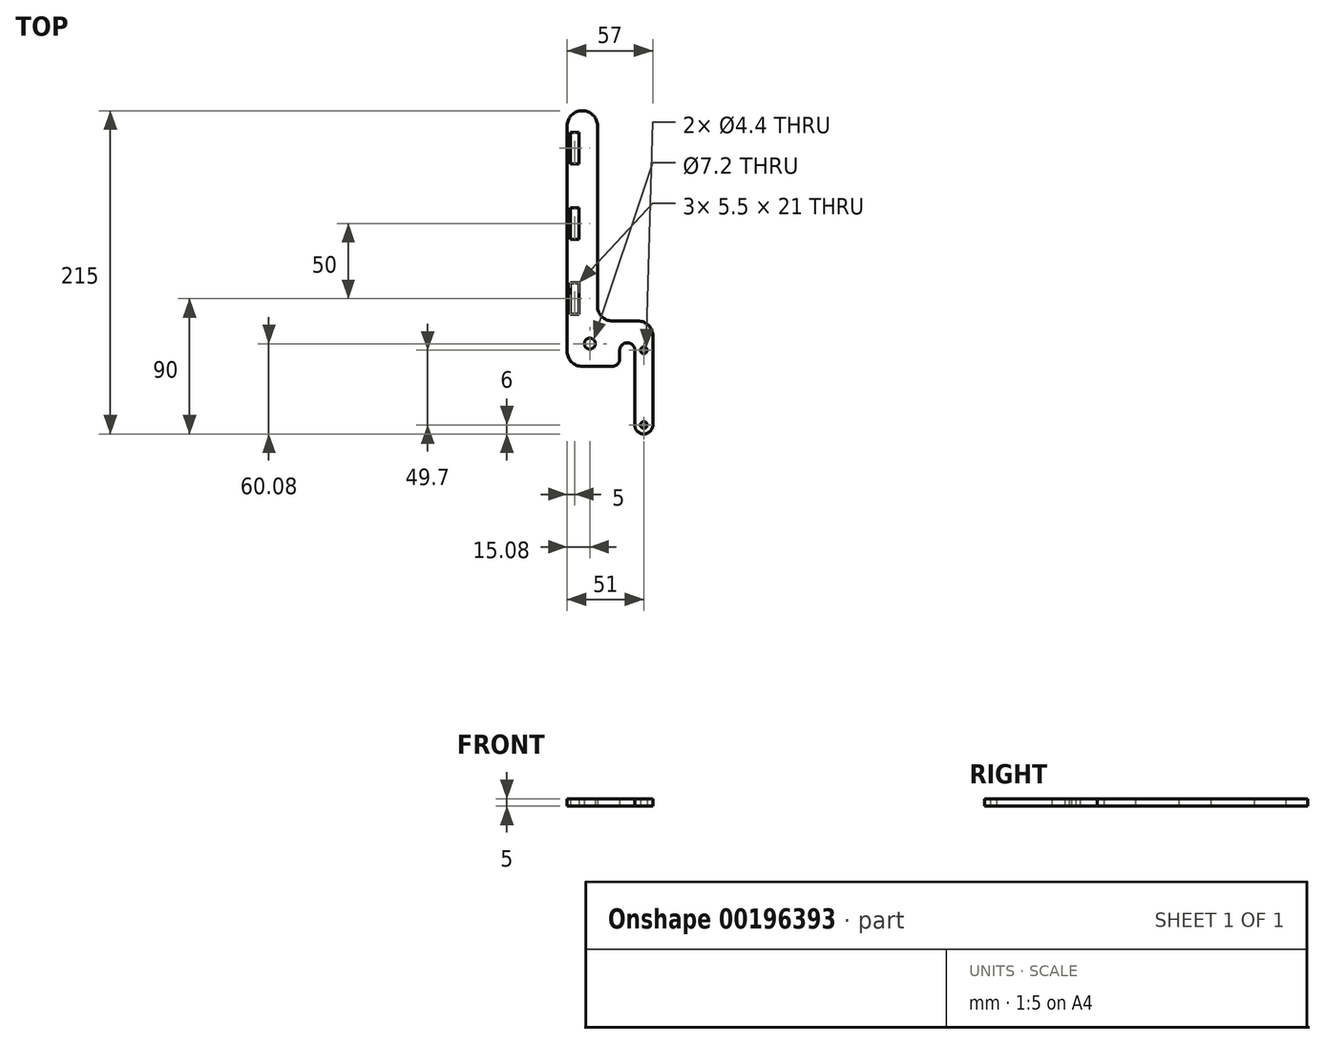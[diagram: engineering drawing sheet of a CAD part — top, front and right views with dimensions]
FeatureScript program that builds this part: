
annotation { "Feature Type Name" : "Feature", "Feature Type Description" : "" }
export const myFeature = defineFeature(function(context is Context, id is Id, definition is map)
    precondition{}
    {
        {
            var Q0;
            Q0=qCreatedBy(makeId("Top.planeOp"),FACE);
            var sketch = newSketch(context, id + "F0", { "sketchPlane" : qUnion([Q0])});
            skLineSegment(sketch, "E0.bottom", {"start": v(0.08, 85) * mm, "end": v(-0.08, 85) * mm});
            skLineSegment(sketch, "E0.top", {"start": v(10.08, -85) * mm, "end": v(-0.08, -85) * mm});
            skLineSegment(sketch, "E0.left", {"start": v(10.08, 75) * mm, "end": v(10.08, -44.84) * mm});
            skLineSegment(sketch, "E0.right", {"start": v(-10.08, 75) * mm, "end": v(-10.08, -75) * mm});
            skPoint(sketch, "E0.middle", {"position": v(0, 0) * mm});
            skLineSegment(sketch, "E1.bottom", {"start": v(-2.33, 49.5) * mm, "end": v(-7.83, 49.5) * mm});
            skLineSegment(sketch, "E1.top", {"start": v(-2.33, 70.5) * mm, "end": v(-7.83, 70.5) * mm});
            skLineSegment(sketch, "E1.left", {"start": v(-2.33, 49.5) * mm, "end": v(-2.33, 70.5) * mm});
            skLineSegment(sketch, "E1.right", {"start": v(-7.83, 49.5) * mm, "end": v(-7.83, 70.5) * mm});
            skPoint(sketch, "E1.middle", {"position": v(-5.08, 60) * mm});
            skLineSegment(sketch, "E2.bottom", {"start": v(-2.33, -0.5) * mm, "end": v(-7.83, -0.5) * mm});
            skLineSegment(sketch, "E2.top", {"start": v(-2.33, 20.5) * mm, "end": v(-7.83, 20.5) * mm});
            skLineSegment(sketch, "E2.left", {"start": v(-2.33, -0.5) * mm, "end": v(-2.33, 20.5) * mm});
            skLineSegment(sketch, "E2.right", {"start": v(-7.83, -0.5) * mm, "end": v(-7.83, 20.5) * mm});
            skPoint(sketch, "E2.middle", {"position": v(-5.08, 10) * mm});
            skLineSegment(sketch, "E3.bottom", {"start": v(-2.33, -50.5) * mm, "end": v(-7.83, -50.5) * mm});
            skLineSegment(sketch, "E3.top", {"start": v(-2.33, -29.5) * mm, "end": v(-7.83, -29.5) * mm});
            skLineSegment(sketch, "E3.left", {"start": v(-2.33, -50.5) * mm, "end": v(-2.33, -29.5) * mm});
            skLineSegment(sketch, "E3.right", {"start": v(-7.83, -50.5) * mm, "end": v(-7.83, -29.5) * mm});
            skPoint(sketch, "E3.middle", {"position": v(-5.08, -40) * mm});
            skCircle(sketch, "E4", {"center": v(5, -69.92) * mm, "radius": 3.6 * mm});
            skCircle(sketch, "E5", {"center": v(40.92, -74.3) * mm, "radius": 2.2 * mm});
            skLineSegment(sketch, "E6.bottom", {"start": v(10.08, -85) * mm, "end": v(19.92, -85) * mm});
            skLineSegment(sketch, "E6.top", {"start": v(20.08, -54.84) * mm, "end": v(34.92, -54.84) * mm});
            skLineSegment(sketch, "E7.bottom", {"start": v(34.92, -54.84) * mm, "end": v(36.92, -54.84) * mm});
            skLineSegment(sketch, "E7.top", {"start": v(40.92, -130) * mm, "end": v(40.92, -130) * mm});
            skLineSegment(sketch, "E7.left", {"start": v(34.92, -74.3) * mm, "end": v(34.92, -124) * mm});
            skLineSegment(sketch, "E7.right", {"start": v(46.92, -64.84) * mm, "end": v(46.92, -124) * mm});
            skPoint(sketch, "E8.visualSharp", {"position": v(-10.08, -85) * mm});
            skArc(sketch, "E8.filletArc", {"start": v(-10.08, -75) * mm, "mid": v(-7.15, -82.07) * mm, "end": v(-0.08, -85) * mm});
            skPoint(sketch, "E9.visualSharp", {"position": v(10.08, -54.84) * mm});
            skArc(sketch, "E9.filletArc", {"start": v(10.08, -44.84) * mm, "mid": v(13, -51.91) * mm, "end": v(20.08, -54.84) * mm});
            skPoint(sketch, "E10.visualSharp", {"position": v(46.92, -54.84) * mm});
            skArc(sketch, "E10.filletArc", {"start": v(46.92, -64.84) * mm, "mid": v(44, -57.77) * mm, "end": v(36.92, -54.84) * mm});
            skPoint(sketch, "E11.visualSharp", {"position": v(-10.08, 85) * mm});
            skArc(sketch, "E11.filletArc", {"start": v(-0.08, 85) * mm, "mid": v(-7.15, 82.07) * mm, "end": v(-10.08, 75) * mm});
            skPoint(sketch, "E12.visualSharp", {"position": v(10.08, 85) * mm});
            skArc(sketch, "E12.filletArc", {"start": v(10.08, 75) * mm, "mid": v(7.15, 82.07) * mm, "end": v(0.08, 85) * mm});
            skCircle(sketch, "E13", {"center": v(40.92, -124) * mm, "radius": 2.2 * mm});
            skPoint(sketch, "E14.visualSharp", {"position": v(34.92, -130) * mm});
            skArc(sketch, "E14.filletArc", {"start": v(34.92, -124) * mm, "mid": v(36.68, -128.24) * mm, "end": v(40.92, -130) * mm});
            skPoint(sketch, "E15.visualSharp", {"position": v(46.92, -130) * mm});
            skArc(sketch, "E15.filletArc", {"start": v(40.92, -130) * mm, "mid": v(45.16, -128.24) * mm, "end": v(46.92, -124) * mm});
            skArc(sketch, "E16", {"start": v(34.92, -74.3) * mm, "mid": v(29.9, -69.3) * mm, "end": v(24.92, -74.34) * mm});
            skLineSegment(sketch, "E17", {"start": v(24.92, -74.26) * mm, "end": v(24.92, -80) * mm});
            skPoint(sketch, "E18.visualSharp", {"position": v(24.92, -85) * mm});
            skArc(sketch, "E18.filletArc", {"start": v(19.92, -85) * mm, "mid": v(23.46, -83.54) * mm, "end": v(24.92, -80) * mm});
            skSolve(sketch);
        }
        {
            var Q0;
            Q0=makeQuery(id+"F0.imprint","IMPRINT",FACE,{"disambiguationData":[TD([[makeQuery(id+"F0.imprint","IMPRINT",EDGE,{"derivedFrom":sQuery(id+"F0.wireOp",EDGE,"E0.bottom")}),1.0]])]});
            extrude(context, id + "F1", {"entities" : qUnion([Q0]), "depth" : 5 * mm});
        }
    });
